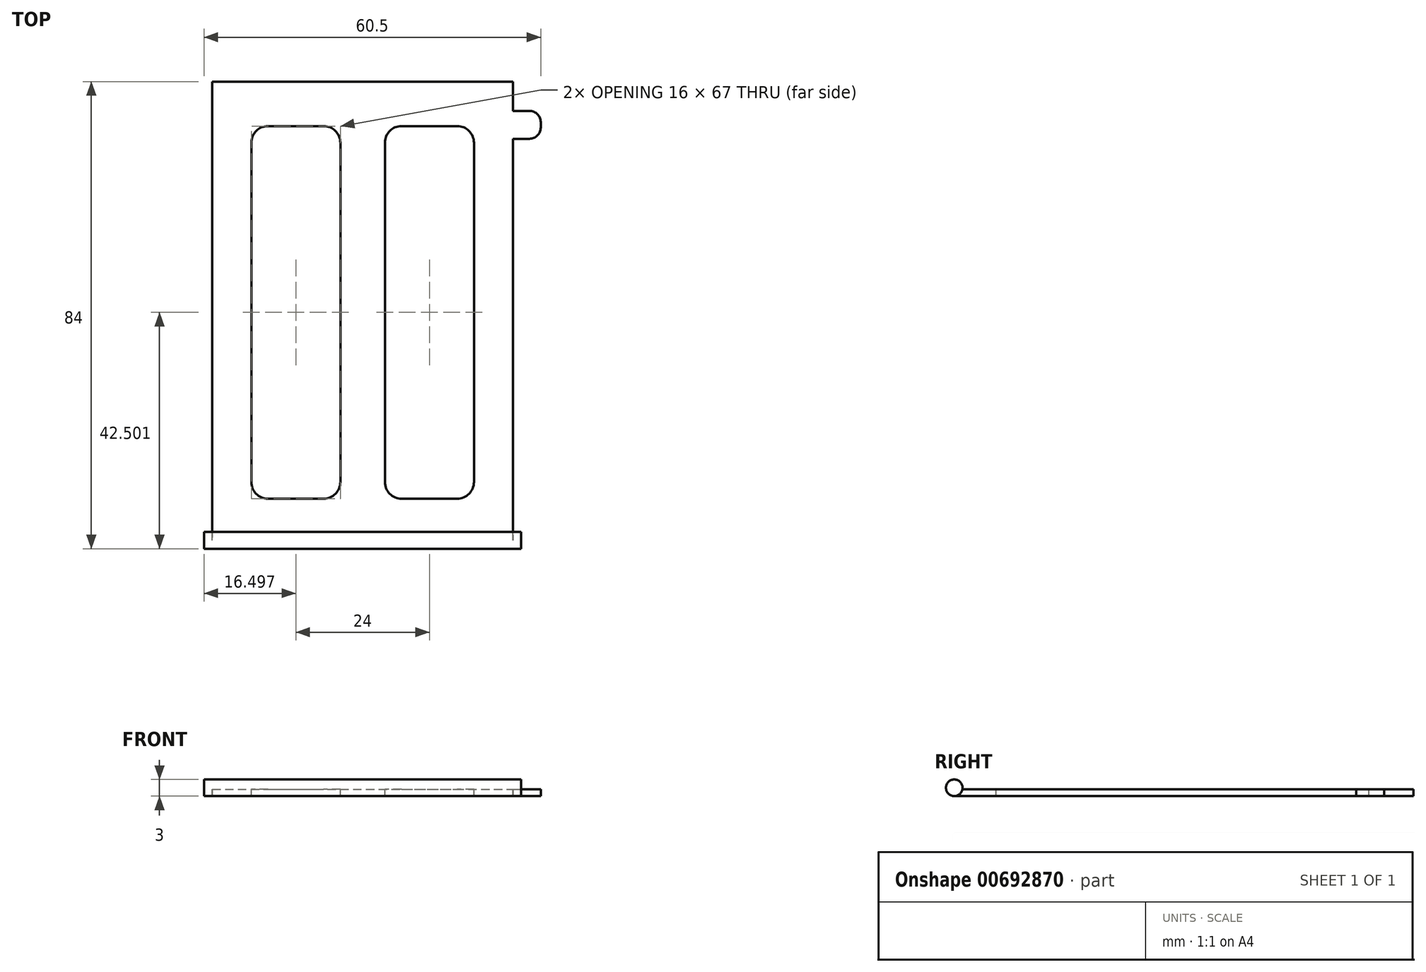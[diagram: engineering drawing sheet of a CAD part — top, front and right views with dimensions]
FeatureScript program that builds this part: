
annotation { "Feature Type Name" : "Feature", "Feature Type Description" : "" }
export const myFeature = defineFeature(function(context is Context, id is Id, definition is map)
    precondition{}
    {
        {
            var Q0;
            Q0=qCreatedBy(makeId("Top.planeOp"),FACE);
            var sketch = newSketch(context, id + "F0", { "sketchPlane" : qUnion([Q0])});
            skLineSegment(sketch, "E0.bottom", {"start": v(-31.2, 29.6) * mm, "end": v(22.8, 29.6) * mm});
            skLineSegment(sketch, "E0.top", {"start": v(-31.2, -54.4) * mm, "end": v(22.8, -54.4) * mm});
            skLineSegment(sketch, "E0.left", {"start": v(-31.2, 29.6) * mm, "end": v(-31.2, -54.4) * mm});
            skLineSegment(sketch, "E0.right", {"start": v(22.8, 29.6) * mm, "end": v(22.8, -54.4) * mm});
            skLineSegment(sketch, "E1.bottom", {"start": v(22.8, 24.31) * mm, "end": v(27.8, 24.31) * mm});
            skLineSegment(sketch, "E1.top", {"start": v(22.8, 19.31) * mm, "end": v(27.8, 19.31) * mm});
            skLineSegment(sketch, "E1.left", {"start": v(22.8, 24.31) * mm, "end": v(22.8, 19.31) * mm});
            skLineSegment(sketch, "E1.right", {"start": v(27.8, 24.31) * mm, "end": v(27.8, 19.31) * mm});
            skLineSegment(sketch, "E2.bottom", {"start": v(-32.7, -51.4) * mm, "end": v(24.3, -51.4) * mm});
            skLineSegment(sketch, "E2.top", {"start": v(-32.7, -54.4) * mm, "end": v(24.3, -54.4) * mm});
            skLineSegment(sketch, "E2.left", {"start": v(-32.7, -51.4) * mm, "end": v(-32.7, -54.4) * mm});
            skLineSegment(sketch, "E2.right", {"start": v(24.3, -51.4) * mm, "end": v(24.3, -54.4) * mm});
            skSolve(sketch);
        }
        {
            var Q0;
            {var subQ4=sQuery(id+"F0.wireOp",EDGE,"E0.bottom");Q0=makeQuery(id+"F0.imprint","IMPRINT",FACE,{"disambiguationData":[TD([[makeQuery(id+"F0.imprint","IMPRINT",EDGE,{"derivedFrom":subQ4}),-1.0]])]});}
            var Q1;
            Q1=makeQuery(id+"F0.imprint","IMPRINT",FACE,{"disambiguationData":[TD([[makeQuery(id+"F0.imprint","IMPRINT",EDGE,{"derivedFrom":sQuery(id+"F0.wireOp",EDGE,"E1.bottom")}),-1.0]])]});
            extrude(context, id + "F1", {"entities" : qUnion([Q0, Q1]), "depth" : 1.2 * mm, "offsetDistance" : 25 * mm});
        }
        {
            var Q0;
            {var subQ5=sQuery(id+"F0.wireOp",EDGE,"E2.left");Q0=makeQuery(id+"F0.imprint","IMPRINT",FACE,{"disambiguationData":[TD([[makeQuery(id+"F0.imprint","IMPRINT",EDGE,{"derivedFrom":subQ5}),1.0]])]});}
            var Q1;
            {var subQ0=sQuery(id+"F0.wireOp",EDGE,"E2.top");var subQ1=sQuery(id+"F0.wireOp",EDGE,"E0.left");var subQ2=makeQuery(id+"F0.imprint","INTERSECT",VERTEX,{"derivedFrom":[subQ1,subQ0]});Q1=makeQuery(id+"F0.imprint","IMPRINT",FACE,{"disambiguationData":[TD([[makeQuery(id+"F0.imprint","IMPRINT",EDGE,{"disambiguationData":[TD([[subQ2,1.0]])],"derivedFrom":subQ1}),1.0]])]});}
            var Q2;
            {var subQ5=sQuery(id+"F0.wireOp",EDGE,"E2.right");Q2=makeQuery(id+"F0.imprint","IMPRINT",FACE,{"disambiguationData":[TD([[makeQuery(id+"F0.imprint","IMPRINT",EDGE,{"derivedFrom":subQ5}),-1.0]])]});}
            extrude(context, id + "F2", {"entities" : qUnion([Q0, Q1, Q2]), "operationType" : NewBodyOperationType.ADD, "depth" : 3 * mm, "offsetDistance" : 25 * mm});
        }
        {
            var Q0;
            Q0=makeQuery(id+"F1.opExtrude","CAP_FACE",FACE,{"disambiguationData":[OSD([sQuery(id+"F0.wireOp",EDGE,"E0.bottom"),sQuery(id+"F0.wireOp",EDGE,"E0.left"),sQuery(id+"F0.wireOp",EDGE,"E0.right"),sQuery(id+"F0.wireOp",EDGE,"E1.bottom"),sQuery(id+"F0.wireOp",EDGE,"E1.top"),sQuery(id+"F0.wireOp",EDGE,"E1.right"),sQuery(id+"F0.wireOp",EDGE,"E2.bottom")])],"isStart":false});
            var sketch = newSketch(context, id + "F3", { "sketchPlane" : qUnion([Q0])});
            skLineSegment(sketch, "E3.bottom", {"start": v(-24.2, 21.6) * mm, "end": v(-8.2, 21.6) * mm});
            skLineSegment(sketch, "E3.top", {"start": v(-24.2, -45.4) * mm, "end": v(-8.2, -45.4) * mm});
            skLineSegment(sketch, "E3.left", {"start": v(-24.2, 21.6) * mm, "end": v(-24.2, -45.4) * mm});
            skLineSegment(sketch, "E3.right", {"start": v(-8.2, 21.6) * mm, "end": v(-8.2, -45.4) * mm});
            skLineSegment(sketch, "E4.bottom", {"start": v(-0.2, 21.6) * mm, "end": v(15.8, 21.6) * mm});
            skLineSegment(sketch, "E4.top", {"start": v(-0.2, -45.4) * mm, "end": v(15.8, -45.4) * mm});
            skLineSegment(sketch, "E4.left", {"start": v(-0.2, 21.6) * mm, "end": v(-0.2, -45.4) * mm});
            skLineSegment(sketch, "E4.right", {"start": v(15.8, 21.6) * mm, "end": v(15.8, -45.4) * mm});
            skSolve(sketch);
        }
        {
            var Q0;
            Q0=makeQuery(id+"F3.imprint","IMPRINT",FACE,{"disambiguationData":[TD([[makeQuery(id+"F3.imprint","IMPRINT",EDGE,{"derivedFrom":sQuery(id+"F3.wireOp",EDGE,"E3.bottom")}),-1.0]])]});
            var Q1;
            Q1=makeQuery(id+"F3.imprint","IMPRINT",FACE,{"disambiguationData":[TD([[makeQuery(id+"F3.imprint","IMPRINT",EDGE,{"derivedFrom":sQuery(id+"F3.wireOp",EDGE,"E4.bottom")}),-1.0]])]});
            extrude(context, id + "F4", {"entities" : qUnion([Q0, Q1]), "operationType" : NewBodyOperationType.REMOVE, "oppositeDirection" : true, "depth" : 25 * mm, "offsetDistance" : 25 * mm});
        }
        {
            var Q0;
            Q0=makeQuery(id+"F4.boolean.opBoolean","COPY",EDGE,{"derivedFrom":makeQuery(id+"F4.opExtrude","SWEPT_EDGE",EDGE,{"disambiguationData":[OSD([sQuery(id+"F3.wireOp",EDGE,"E3.bottom"),sQuery(id+"F3.wireOp",EDGE,"E3.right")])]})});
            var Q1;
            Q1=makeQuery(id+"F4.boolean.opBoolean","COPY",EDGE,{"derivedFrom":makeQuery(id+"F4.opExtrude","SWEPT_EDGE",EDGE,{"disambiguationData":[OSD([sQuery(id+"F3.wireOp",EDGE,"E4.bottom"),sQuery(id+"F3.wireOp",EDGE,"E4.right")])]})});
            var Q2;
            Q2=makeQuery(id+"F4.boolean.opBoolean","COPY",EDGE,{"derivedFrom":makeQuery(id+"F4.opExtrude","SWEPT_EDGE",EDGE,{"disambiguationData":[OSD([sQuery(id+"F3.wireOp",EDGE,"E4.bottom"),sQuery(id+"F3.wireOp",EDGE,"E4.left")])]})});
            var Q3;
            Q3=makeQuery(id+"F4.boolean.opBoolean","COPY",EDGE,{"derivedFrom":makeQuery(id+"F4.opExtrude","SWEPT_EDGE",EDGE,{"disambiguationData":[OSD([sQuery(id+"F3.wireOp",EDGE,"E3.bottom"),sQuery(id+"F3.wireOp",EDGE,"E3.left")])]})});
            var Q4;
            Q4=makeQuery(id+"F4.boolean.opBoolean","COPY",EDGE,{"derivedFrom":makeQuery(id+"F4.opExtrude","SWEPT_EDGE",EDGE,{"disambiguationData":[OSD([sQuery(id+"F3.wireOp",EDGE,"E3.top"),sQuery(id+"F3.wireOp",EDGE,"E3.left")])]})});
            var Q5;
            Q5=makeQuery(id+"F4.boolean.opBoolean","COPY",EDGE,{"derivedFrom":makeQuery(id+"F4.opExtrude","SWEPT_EDGE",EDGE,{"disambiguationData":[OSD([sQuery(id+"F3.wireOp",EDGE,"E4.top"),sQuery(id+"F3.wireOp",EDGE,"E4.left")])]})});
            var Q6;
            Q6=makeQuery(id+"F4.boolean.opBoolean","COPY",EDGE,{"derivedFrom":makeQuery(id+"F4.opExtrude","SWEPT_EDGE",EDGE,{"disambiguationData":[OSD([sQuery(id+"F3.wireOp",EDGE,"E3.top"),sQuery(id+"F3.wireOp",EDGE,"E3.right")])]})});
            var Q7;
            Q7=makeQuery(id+"F4.boolean.opBoolean","COPY",EDGE,{"derivedFrom":makeQuery(id+"F4.opExtrude","SWEPT_EDGE",EDGE,{"disambiguationData":[OSD([sQuery(id+"F3.wireOp",EDGE,"E4.top"),sQuery(id+"F3.wireOp",EDGE,"E4.right")])]})});
            fillet(context, id + "F5", {"entities" : qUnion([Q0, Q1, Q2, Q3, Q4, Q5, Q6, Q7]), "radius" : 3 * mm, "tangentPropagation" : true, "allowEdgeOverflow" : false});
        }
        {
            var Q0;
            Q0=makeQuery(id+"F1.opExtrude","SWEPT_EDGE",EDGE,{"disambiguationData":[OSD([sQuery(id+"F0.wireOp",EDGE,"E1.top"),sQuery(id+"F0.wireOp",EDGE,"E1.right")])]});
            var Q1;
            Q1=makeQuery(id+"F1.opExtrude","SWEPT_EDGE",EDGE,{"disambiguationData":[OSD([sQuery(id+"F0.wireOp",EDGE,"E1.bottom"),sQuery(id+"F0.wireOp",EDGE,"E1.right")])]});
            fillet(context, id + "F6", {"entities" : qUnion([Q0, Q1]), "radius" : 2 * mm, "tangentPropagation" : true, "allowEdgeOverflow" : false});
        }
        {
            var Q0;
            Q0=makeQuery(id+"F2.opExtrude","CAP_EDGE",EDGE,{"disambiguationData":[OSD([sQuery(id+"F0.wireOp",EDGE,"E2.bottom")])],"isStart":false});
            var Q1;
            Q1=makeQuery(id+"F2.opExtrude","CAP_EDGE",EDGE,{"disambiguationData":[OSD([sQuery(id+"F0.wireOp",EDGE,"E2.top")])],"isStart":false});
            var Q2;
            {var subQ1=sQuery(id+"F0.wireOp",EDGE,"E2.bottom");var subQ2=sQuery(id+"F0.wireOp",EDGE,"E0.left");Q2=makeQuery(id+"F2.boolean.opBoolean","SPLIT",EDGE,{"disambiguationData":[TD([makeQuery(id+"F1.opExtrude","SWEPT_FACE",FACE,{"disambiguationData":[OSD([subQ2])]})])],"derivedFrom":makeQuery(id+"F2.opExtrude","CAP_EDGE",EDGE,{"disambiguationData":[OSD([subQ1])],"isStart":true})});}
            var Q3;
            Q3=makeQuery(id+"F2.opExtrude","CAP_EDGE",EDGE,{"disambiguationData":[OSD([sQuery(id+"F0.wireOp",EDGE,"E2.top")])],"isStart":true});
            fillet(context, id + "F7", {"entities" : qUnion([Q0, Q1, Q2, Q3]), "radius" : 1.5 * mm, "tangentPropagation" : true, "allowEdgeOverflow" : false});
        }
    });
